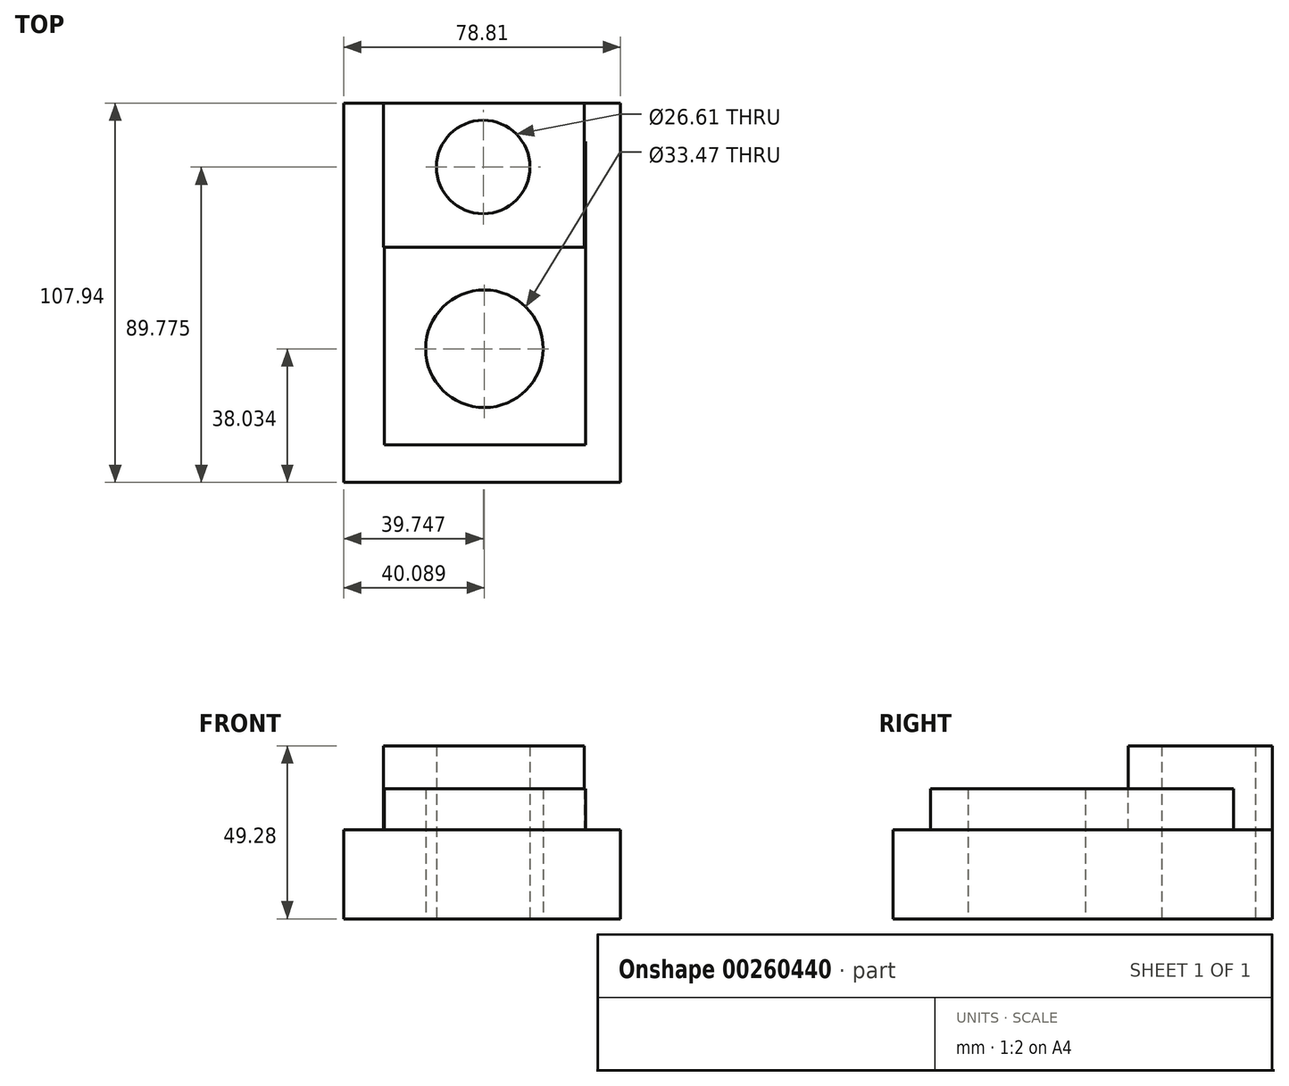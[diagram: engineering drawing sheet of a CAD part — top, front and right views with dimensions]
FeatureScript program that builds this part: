
annotation { "Feature Type Name" : "Feature", "Feature Type Description" : "" }
export const myFeature = defineFeature(function(context is Context, id is Id, definition is map)
    precondition{}
    {
        {
            var Q0;
            Q0=qCreatedBy(makeId("Top.planeOp"),FACE);
            var sketch = newSketch(context, id + "F0", { "sketchPlane" : qUnion([Q0])});
            skLineSegment(sketch, "E0.bottom", {"start": v(-36.32, 40.95) * mm, "end": v(42.49, 40.95) * mm});
            skLineSegment(sketch, "E0.top", {"start": v(-36.32, -67) * mm, "end": v(42.49, -67) * mm});
            skLineSegment(sketch, "E0.left", {"start": v(-36.32, 40.95) * mm, "end": v(-36.32, -67) * mm});
            skLineSegment(sketch, "E0.right", {"start": v(42.49, 40.95) * mm, "end": v(42.49, -67) * mm});
            skSolve(sketch);
        }
        {
            var Q0;
            Q0 = qSketchRegion(id + "F0", true);
            extrude(context, id + "F1", {"entities" : qUnion([Q0]), "depth" : 25.4 * mm});
        }
        {
            var Q0;
            Q0=qCreatedBy(makeId("Top.planeOp"),FACE);
            var sketch = newSketch(context, id + "F2", { "sketchPlane" : qUnion([Q0])});
            skLineSegment(sketch, "E1.bottom", {"start": v(-24.67, 29.98) * mm, "end": v(32.55, 29.98) * mm});
            skLineSegment(sketch, "E1.top", {"start": v(-24.67, -56.37) * mm, "end": v(32.55, -56.37) * mm});
            skLineSegment(sketch, "E1.left", {"start": v(-24.67, 29.98) * mm, "end": v(-24.67, -56.37) * mm});
            skLineSegment(sketch, "E1.right", {"start": v(32.55, 29.98) * mm, "end": v(32.55, -56.37) * mm});
            skSolve(sketch);
        }
        {
            var Q0;
            Q0 = qSketchRegion(id + "F2", true);
            extrude(context, id + "F3", {"entities" : qUnion([Q0]), "operationType" : NewBodyOperationType.ADD, "depth" : 37.08 * mm});
        }
        {
            var Q0;
            Q0=qCreatedBy(makeId("Top.planeOp"),FACE);
            var sketch = newSketch(context, id + "F4", { "sketchPlane" : qUnion([Q0])});
            skLineSegment(sketch, "E2.bottom", {"start": v(-25.01, 40.95) * mm, "end": v(32.2, 40.95) * mm});
            skLineSegment(sketch, "E2.top", {"start": v(-25.01, 0) * mm, "end": v(32.2, 0) * mm});
            skLineSegment(sketch, "E2.left", {"start": v(-25.01, 40.95) * mm, "end": v(-25.01, 0) * mm});
            skLineSegment(sketch, "E2.right", {"start": v(32.2, 40.95) * mm, "end": v(32.2, 0) * mm});
            skSolve(sketch);
        }
        {
            var Q0;
            Q0 = qSketchRegion(id + "F4", true);
            extrude(context, id + "F5", {"entities" : qUnion([Q0]), "operationType" : NewBodyOperationType.ADD, "depth" : 49.28 * mm});
        }
        {
            var Q0;
            Q0=qCreatedBy(makeId("Top.planeOp"),FACE);
            var sketch = newSketch(context, id + "F6", { "sketchPlane" : qUnion([Q0])});
            skCircle(sketch, "E3", {"center": v(3.43, 22.78) * mm, "radius": 13.3 * mm});
            skSolve(sketch);
        }
        {
            var Q0;
            Q0=qCreatedBy(makeId("Top.planeOp"),FACE);
            var sketch = newSketch(context, id + "F7", { "sketchPlane" : qUnion([Q0])});
            skCircle(sketch, "E4", {"center": v(3.77, -28.96) * mm, "radius": 16.73 * mm});
            skSolve(sketch);
        }
        {
            var Q0;
            Q0 = qSketchRegion(id + "F6", true);
            extrude(context, id + "F8", {"entities" : qUnion([Q0]), "operationType" : NewBodyOperationType.REMOVE, "depth" : 92.46 * mm});
        }
        {
            var Q0;
            Q0 = qSketchRegion(id + "F7", true);
            extrude(context, id + "F9", {"entities" : qUnion([Q0]), "operationType" : NewBodyOperationType.REMOVE, "depth" : 76.96 * mm});
        }
    });
